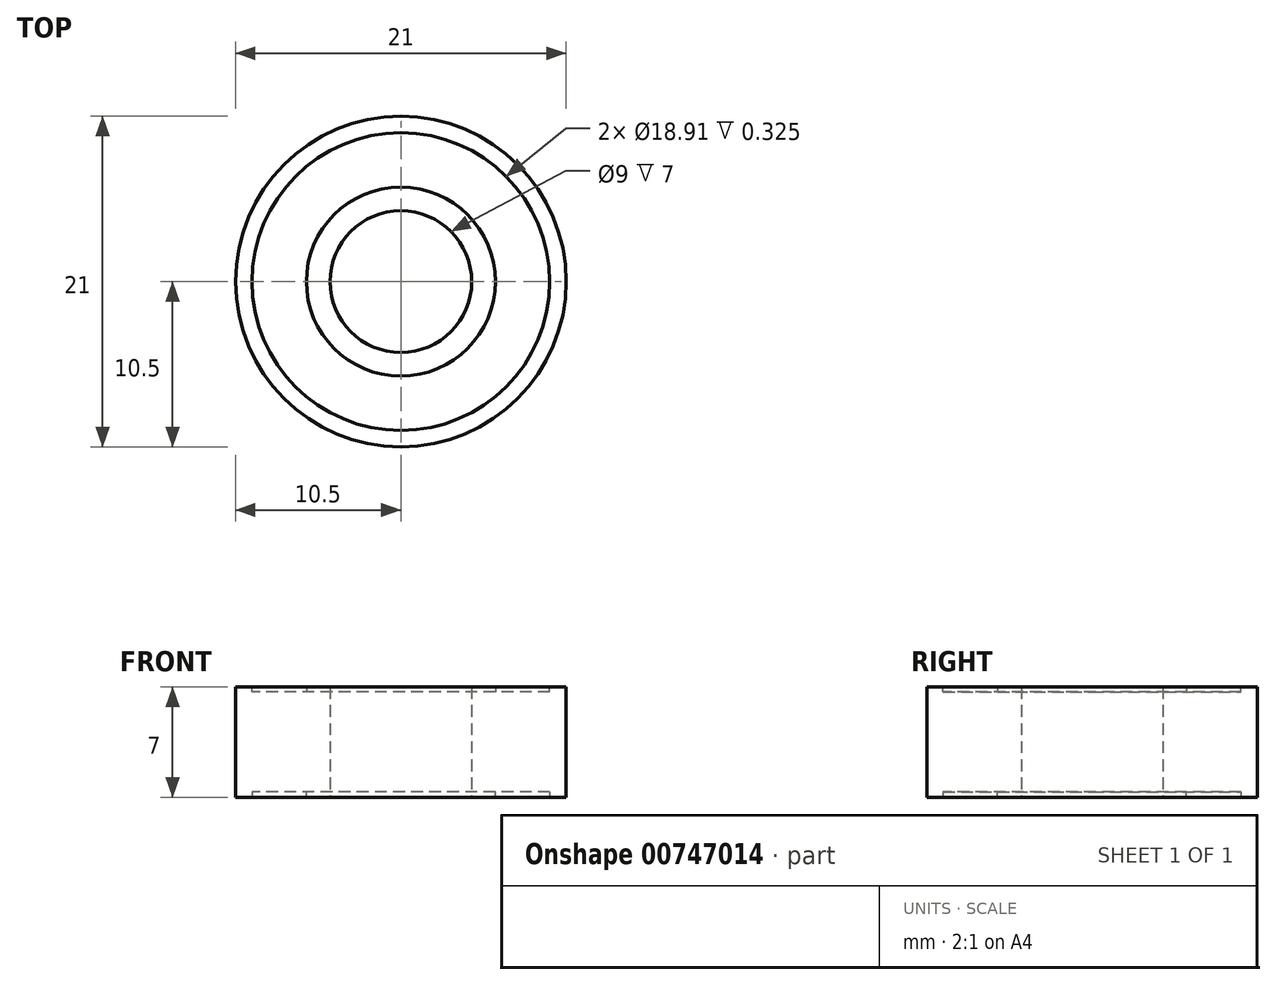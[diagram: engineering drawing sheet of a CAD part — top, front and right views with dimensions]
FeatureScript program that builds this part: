
annotation { "Feature Type Name" : "Feature", "Feature Type Description" : "" }
export const myFeature = defineFeature(function(context is Context, id is Id, definition is map)
    precondition{}
    {
        {
            var Q0;
            Q0=qCreatedBy(makeId("Top.planeOp"),FACE);
            var sketch = newSketch(context, id + "F0", { "sketchPlane" : qUnion([Q0])});
            skCircle(sketch, "E0", {"center": v(0, 0) * mm, "radius": 10.5 * mm});
            skSolve(sketch);
        }
        {
            var Q0;
            Q0=makeQuery(id+"F0.imprint","IMPRINT",FACE,{"disambiguationData":[TD([[makeQuery(id+"F0.imprint","IMPRINT",EDGE,{"derivedFrom":sQuery(id+"F0.wireOp",EDGE,"E0")}),1.0]])]});
            extrude(context, id + "F1", {"entities" : qUnion([Q0]), "depth" : 3.5 * mm, "offsetDistance" : 25.4 * mm});
        }
        {
            var Q0;
            Q0=makeQuery(id+"F1.opExtrude","CAP_FACE",FACE,{"disambiguationData":[OSD([sQuery(id+"F0.wireOp",EDGE,"E0")])],"isStart":false});
            var sketch = newSketch(context, id + "F2", { "sketchPlane" : qUnion([Q0])});
            skCircle(sketch, "E1", {"center": v(0, 0) * mm, "radius": 9.45 * mm});
            skSolve(sketch);
        }
        {
            var Q0;
            Q0=makeQuery(id+"F2.imprint","IMPRINT",FACE,{"disambiguationData":[TD([[makeQuery(id+"F2.imprint","IMPRINT",EDGE,{"derivedFrom":sQuery(id+"F2.wireOp",EDGE,"E1")}),1.0]])]});
            extrude(context, id + "F3", {"entities" : qUnion([Q0]), "operationType" : NewBodyOperationType.REMOVE, "oppositeDirection" : true, "depth" : 25.4 * mm, "offsetDistance" : 25.4 * mm});
        }
        {
            var Q0;
            Q0=qCreatedBy(makeId("Top.planeOp"),FACE);
            var sketch = newSketch(context, id + "F4", { "sketchPlane" : qUnion([Q0])});
            skCircle(sketch, "E2", {"center": v(0, 0) * mm, "radius": 9.45 * mm});
            skSolve(sketch);
        }
        {
            var Q0;
            Q0=makeQuery(id+"F4.imprint","IMPRINT",FACE,{"disambiguationData":[TD([[makeQuery(id+"F4.imprint","IMPRINT",EDGE,{"derivedFrom":sQuery(id+"F4.wireOp",EDGE,"E2")}),1.0]])]});
            extrude(context, id + "F5", {"entities" : qUnion([Q0]), "operationType" : NewBodyOperationType.ADD, "depth" : 3.17 * mm, "offsetDistance" : 25.4 * mm});
        }
        {
            var Q0;
            Q0=qCreatedBy(makeId("Top.planeOp"),FACE);
            var sketch = newSketch(context, id + "F6", { "sketchPlane" : qUnion([Q0])});
            skCircle(sketch, "E3", {"center": v(0, 0) * mm, "radius": 6 * mm});
            skSolve(sketch);
        }
        {
            var Q0;
            Q0 = qSketchRegion(id + "F6", true);
            extrude(context, id + "F7", {"entities" : qUnion([Q0]), "operationType" : NewBodyOperationType.ADD, "depth" : 3.5 * mm, "offsetDistance" : 25.4 * mm});
        }
        {
            var Q0;
            Q0=makeQuery(id+"F7.opExtrude","CAP_FACE",FACE,{"disambiguationData":[OSD([sQuery(id+"F6.wireOp",EDGE,"E3")])],"isStart":false});
            shell(context, id + "F8", {"entities" : qUnion([Q0]), "thickness" : 1.96 * mm});
        }
        {
            var Q0;
            Q0=qCreatedBy(makeId("Top.planeOp"),FACE);
            var sketch = newSketch(context, id + "F9", { "sketchPlane" : qUnion([Q0])});
            skCircle(sketch, "E4", {"center": v(0, 0) * mm, "radius": 4.5 * mm});
            skSolve(sketch);
        }
        {
            var Q0;
            Q0 = qSketchRegion(id + "F9", true);
            extrude(context, id + "F10", {"entities" : qUnion([Q0]), "operationType" : NewBodyOperationType.REMOVE, "depth" : 2514.6 * mm, "offsetDistance" : 25.4 * mm});
        }
        {
            var Q0;
            Q0=makeQuery(id+"F1.opExtrude","SWEPT_BODY",BODY,{"disambiguationData":[OSD([sQuery(id+"F0.wireOp",EDGE,"E0")])]});
            var Q1;
            Q1=qCreatedBy(makeId("Top.planeOp"),FACE);
            mirror(context, id + "F11", {"operationType" : NewBodyOperationType.ADD, "entities" : qUnion([Q0]), "mirrorPlane" : qUnion([Q1])});
        }
    });
